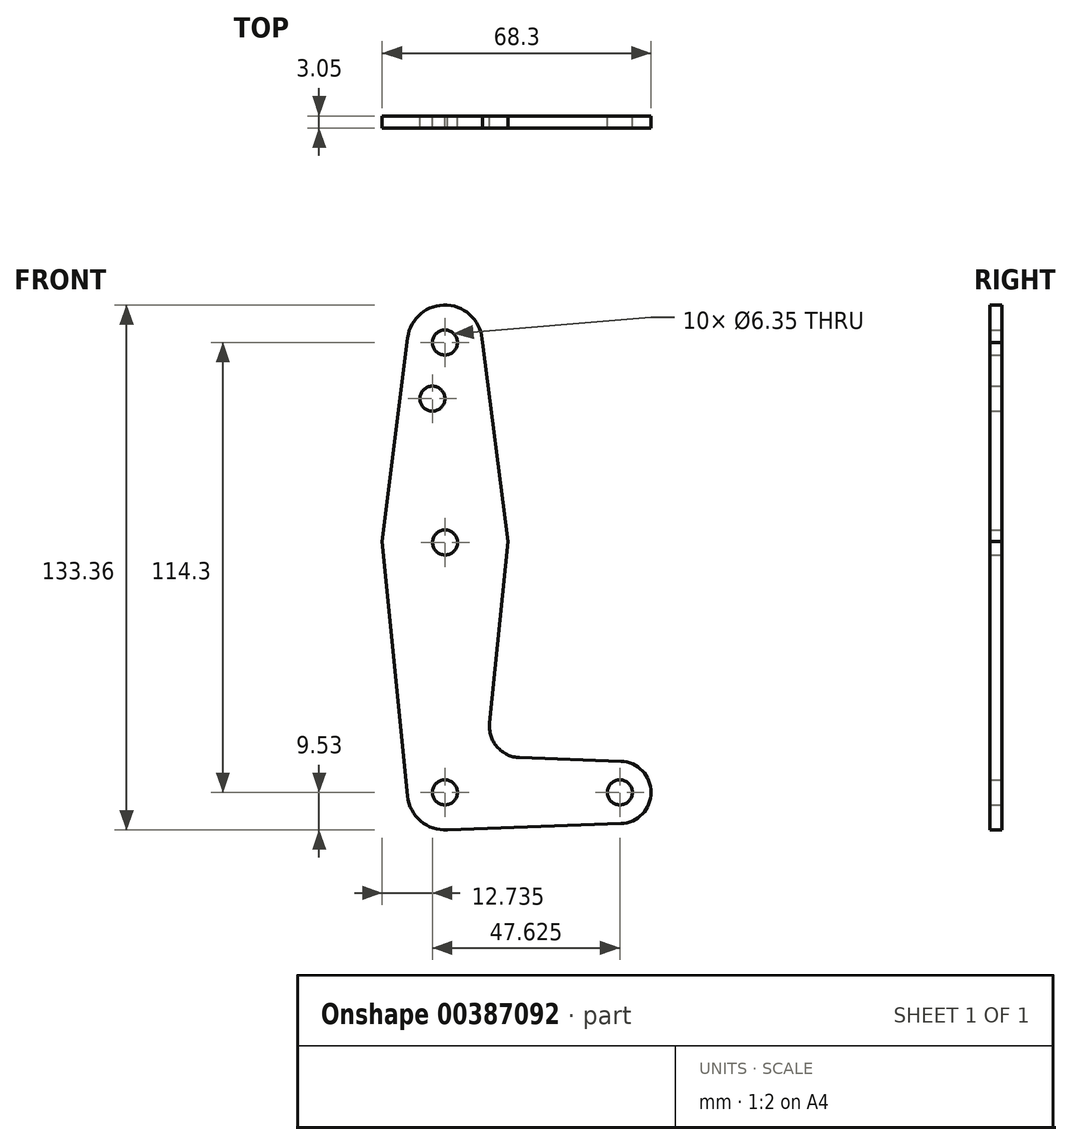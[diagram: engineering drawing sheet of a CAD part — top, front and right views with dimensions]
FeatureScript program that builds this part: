
annotation { "Feature Type Name" : "Feature", "Feature Type Description" : "" }
export const myFeature = defineFeature(function(context is Context, id is Id, definition is map)
    precondition{}
    {
        {
            var Q0;
            Q0=qCreatedBy(makeId("Front.planeOp"),FACE);
            var sketch = newSketch(context, id + "F0", { "sketchPlane" : qUnion([Q0])});
            skLineSegment(sketch, "E0", {"start": v(0, 0) * mm, "end": v(0, 28.38) * mm, "construction": true});
            skLineSegment(sketch, "E1", {"start": v(0, 28.38) * mm, "end": v(0, 114.3) * mm, "construction": true});
            skLineSegment(sketch, "E2", {"start": v(0, 0) * mm, "end": v(44.45, 0) * mm, "construction": true});
            skCircle(sketch, "E3", {"center": v(0, 0) * mm, "radius": 9.53 * mm});
            skCircle(sketch, "E4", {"center": v(0.06, 63.5) * mm, "radius": 15.88 * mm});
            skCircle(sketch, "E5", {"center": v(0, 114.3) * mm, "radius": 9.53 * mm});
            skCircle(sketch, "E6", {"center": v(44.45, 0) * mm, "radius": 7.94 * mm});
            skLineSegment(sketch, "E7", {"start": v(9.53, 114.3) * mm, "end": v(16.04, 63.72) * mm});
            skLineSegment(sketch, "E8", {"start": v(16.04, 63.72) * mm, "end": v(11.36, 17.6) * mm});
            skLineSegment(sketch, "E9", {"start": v(-9.45, 115.48) * mm, "end": v(-15.91, 63.7) * mm});
            skLineSegment(sketch, "E10", {"start": v(-15.91, 63.7) * mm, "end": v(-9.48, -0.94) * mm});
            skLineSegment(sketch, "E11", {"start": v(0, -9.53) * mm, "end": v(44.73, -7.93) * mm});
            skLineSegment(sketch, "E12", {"start": v(18.99, 8.85) * mm, "end": v(44.73, 7.93) * mm});
            skCircle(sketch, "E13", {"center": v(0, 114.3) * mm, "radius": 3.18 * mm});
            skCircle(sketch, "E14", {"center": v(0.06, 63.5) * mm, "radius": 3.18 * mm});
            skCircle(sketch, "E15", {"center": v(0, 0) * mm, "radius": 3.18 * mm});
            skCircle(sketch, "E16", {"center": v(44.45, 0) * mm, "radius": 3.18 * mm});
            skCircle(sketch, "E17", {"center": v(-3.18, 100.03) * mm, "radius": 3.18 * mm});
            skPoint(sketch, "E18.newPointB", {"position": v(0, 9.53) * mm});
            skArc(sketch, "E18.filletArc", {"start": v(11.36, 17.6) * mm, "mid": v(13.28, 11.57) * mm, "end": v(18.99, 8.85) * mm});
            skSolve(sketch);
        }
        {
            var Q0;
            Q0 = qSketchRegion(id + "F0", true);
            extrude(context, id + "F1", {"entities" : qUnion([Q0]), "depth" : 3.05 * mm});
        }
    });
